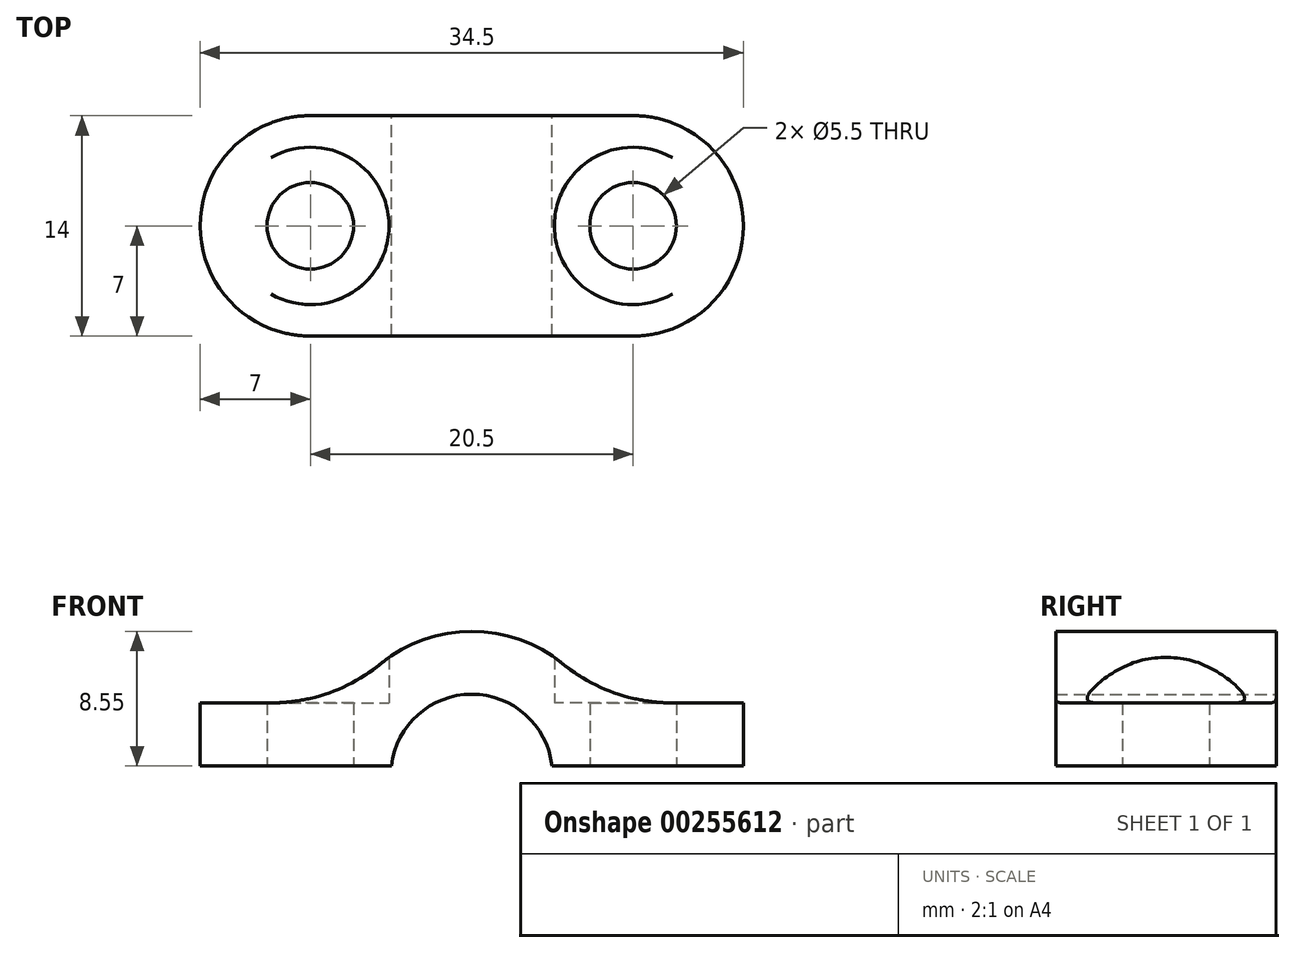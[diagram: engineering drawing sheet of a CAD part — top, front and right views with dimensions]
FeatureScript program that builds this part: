
annotation { "Feature Type Name" : "Feature", "Feature Type Description" : "" }
export const myFeature = defineFeature(function(context is Context, id is Id, definition is map)
    precondition{}
    {
        {
            var Q0;
            Q0=qCreatedBy(makeId("Front.planeOp"),FACE);
            var sketch = newSketch(context, id + "F0", { "sketchPlane" : qUnion([Q0])});
            skArc(sketch, "E0", {"start": v(5.1, 0) * mm, "mid": v(0, 4.55) * mm, "end": v(-5.1, 0) * mm});
            skLineSegment(sketch, "E1", {"start": v(-17.25, 0) * mm, "end": v(-5.1, 0) * mm});
            skLineSegment(sketch, "E2", {"start": v(-17.25, 0) * mm, "end": v(-17.25, 4) * mm});
            skLineSegment(sketch, "E3", {"start": v(-17.25, 4) * mm, "end": v(-7.9, 4) * mm});
            skLineSegment(sketch, "E4.MirrorCS", {"start": v(17.25, 4) * mm, "end": v(7.9, 4) * mm});
            skLineSegment(sketch, "E5.MirrorCS", {"start": v(17.25, 0) * mm, "end": v(17.25, 4) * mm});
            skLineSegment(sketch, "E6.MirrorCS", {"start": v(17.25, 0) * mm, "end": v(5.1, 0) * mm});
            skArc(sketch, "E7.trimOffspring", {"start": v(7.9, 4) * mm, "mid": v(0, 8.55) * mm, "end": v(-7.9, 4) * mm});
            skPoint(sketch, "E8.end.orphan", {"position": v(8.98, 0) * mm});
            skPoint(sketch, "E8.start.orphan", {"position": v(-8.98, 0) * mm});
            skSolve(sketch);
        }
        {
            var Q0;
            Q0 = qSketchRegion(id + "F0", true);
            extrude(context, id + "F1", {"entities" : qUnion([Q0]), "depth" : 14 * mm});
        }
        {
            var Q0;
            Q0=makeQuery(id+"F1.opExtrude","SWEPT_FACE",FACE,{"disambiguationData":[OSD([sQuery(id+"F0.wireOp",EDGE,"E1")])]});
            var sketch = newSketch(context, id + "F2", { "sketchPlane" : qUnion([Q0])});
            skArc(sketch, "E9", {"start": v(-10.25, 14) * mm, "mid": v(-17.25, 7) * mm, "end": v(-10.25, 0) * mm});
            skCircle(sketch, "E10", {"center": v(-10.25, 7) * mm, "radius": 2.75 * mm});
            skCircle(sketch, "E11.MirrorC", {"center": v(10.25, 7) * mm, "radius": 2.75 * mm});
            skArc(sketch, "E12.MirrorCS", {"start": v(10.25, 14) * mm, "mid": v(17.25, 7) * mm, "end": v(10.25, 0) * mm});
            skLineSegment(sketch, "E13", {"start": v(-10.25, 14) * mm, "end": v(10.25, 14) * mm});
            skLineSegment(sketch, "E14", {"start": v(-10.25, 0) * mm, "end": v(10.25, 0) * mm});
            skSolve(sketch);
        }
        {
            var Q0;
            Q0 = qSketchRegion(id + "F2", true);
            extrude(context, id + "F3", {"entities" : qUnion([Q0]), "operationType" : NewBodyOperationType.INTERSECT, "endBound" : BoundingType.THROUGH_ALL, "oppositeDirection" : true, "depth" : 25 * mm});
        }
        {
            var Q0;
            {var subQ0=sQuery(id+"F0.wireOp",EDGE,"E7.trimOffspring");var subQ1=sQuery(id+"F0.wireOp",EDGE,"E3");Q0=makeQuery(id+"F3.boolean.opBoolean","SPLIT",EDGE,{"disambiguationData":[TD([makeQuery(id+"F1.opExtrude","CAP_FACE",FACE,{"disambiguationData":[OSD([sQuery(id+"F0.wireOp",EDGE,"E0"),sQuery(id+"F0.wireOp",EDGE,"E1"),sQuery(id+"F0.wireOp",EDGE,"E2"),subQ1,sQuery(id+"F0.wireOp",EDGE,"E4.MirrorCS"),sQuery(id+"F0.wireOp",EDGE,"E5.MirrorCS"),sQuery(id+"F0.wireOp",EDGE,"E6.MirrorCS"),subQ0])],"isStart":true})])],"derivedFrom":makeQuery(id+"F1.opExtrude","SWEPT_EDGE",EDGE,{"disambiguationData":[OSD([subQ1,subQ0])]})});}
            var Q1;
            {var subQ0=sQuery(id+"F0.wireOp",EDGE,"E7.trimOffspring");var subQ1=sQuery(id+"F0.wireOp",EDGE,"E3");Q1=makeQuery(id+"F3.boolean.opBoolean","SPLIT",EDGE,{"disambiguationData":[TD([makeQuery(id+"F1.opExtrude","CAP_FACE",FACE,{"disambiguationData":[OSD([sQuery(id+"F0.wireOp",EDGE,"E0"),sQuery(id+"F0.wireOp",EDGE,"E1"),sQuery(id+"F0.wireOp",EDGE,"E2"),subQ1,sQuery(id+"F0.wireOp",EDGE,"E4.MirrorCS"),sQuery(id+"F0.wireOp",EDGE,"E5.MirrorCS"),sQuery(id+"F0.wireOp",EDGE,"E6.MirrorCS"),subQ0])],"isStart":false})])],"derivedFrom":makeQuery(id+"F1.opExtrude","SWEPT_EDGE",EDGE,{"disambiguationData":[OSD([subQ1,subQ0])]})});}
            var Q2;
            {var subQ0=sQuery(id+"F0.wireOp",EDGE,"E7.trimOffspring");var subQ1=sQuery(id+"F0.wireOp",EDGE,"E4.MirrorCS");Q2=makeQuery(id+"F3.boolean.opBoolean","SPLIT",EDGE,{"disambiguationData":[TD([makeQuery(id+"F1.opExtrude","CAP_FACE",FACE,{"disambiguationData":[OSD([sQuery(id+"F0.wireOp",EDGE,"E0"),sQuery(id+"F0.wireOp",EDGE,"E1"),sQuery(id+"F0.wireOp",EDGE,"E2"),sQuery(id+"F0.wireOp",EDGE,"E3"),subQ1,sQuery(id+"F0.wireOp",EDGE,"E5.MirrorCS"),sQuery(id+"F0.wireOp",EDGE,"E6.MirrorCS"),subQ0])],"isStart":false})])],"derivedFrom":makeQuery(id+"F1.opExtrude","SWEPT_EDGE",EDGE,{"disambiguationData":[OSD([subQ1,subQ0])]})});}
            var Q3;
            {var subQ0=sQuery(id+"F0.wireOp",EDGE,"E7.trimOffspring");var subQ1=sQuery(id+"F0.wireOp",EDGE,"E4.MirrorCS");Q3=makeQuery(id+"F3.boolean.opBoolean","SPLIT",EDGE,{"disambiguationData":[TD([makeQuery(id+"F1.opExtrude","CAP_FACE",FACE,{"disambiguationData":[OSD([sQuery(id+"F0.wireOp",EDGE,"E0"),sQuery(id+"F0.wireOp",EDGE,"E1"),sQuery(id+"F0.wireOp",EDGE,"E2"),sQuery(id+"F0.wireOp",EDGE,"E3"),subQ1,sQuery(id+"F0.wireOp",EDGE,"E5.MirrorCS"),sQuery(id+"F0.wireOp",EDGE,"E6.MirrorCS"),subQ0])],"isStart":true})])],"derivedFrom":makeQuery(id+"F1.opExtrude","SWEPT_EDGE",EDGE,{"disambiguationData":[OSD([subQ1,subQ0])]})});}
            fillet(context, id + "F4", {"entities" : qUnion([Q0, Q1, Q2, Q3]), "radius" : 11 * mm, "tangentPropagation" : true, "allowEdgeOverflow" : false});
        }
        {
            var Q0;
            Q0=makeQuery(id+"F1.opExtrude","SWEPT_FACE",FACE,{"disambiguationData":[OSD([sQuery(id+"F0.wireOp",EDGE,"E4.MirrorCS")])]});
            var sketch = newSketch(context, id + "F5", { "sketchPlane" : qUnion([Q0])});
            skCircle(sketch, "E15", {"center": v(10.25, -7) * mm, "radius": 5 * mm});
            skCircle(sketch, "E16", {"center": v(-10.25, -7) * mm, "radius": 5 * mm});
            skSolve(sketch);
        }
        {
            var Q0;
            Q0 = qSketchRegion(id + "F5", true);
            extrude(context, id + "F6", {"entities" : qUnion([Q0]), "operationType" : NewBodyOperationType.REMOVE, "depth" : 25 * mm});
        }
    });
